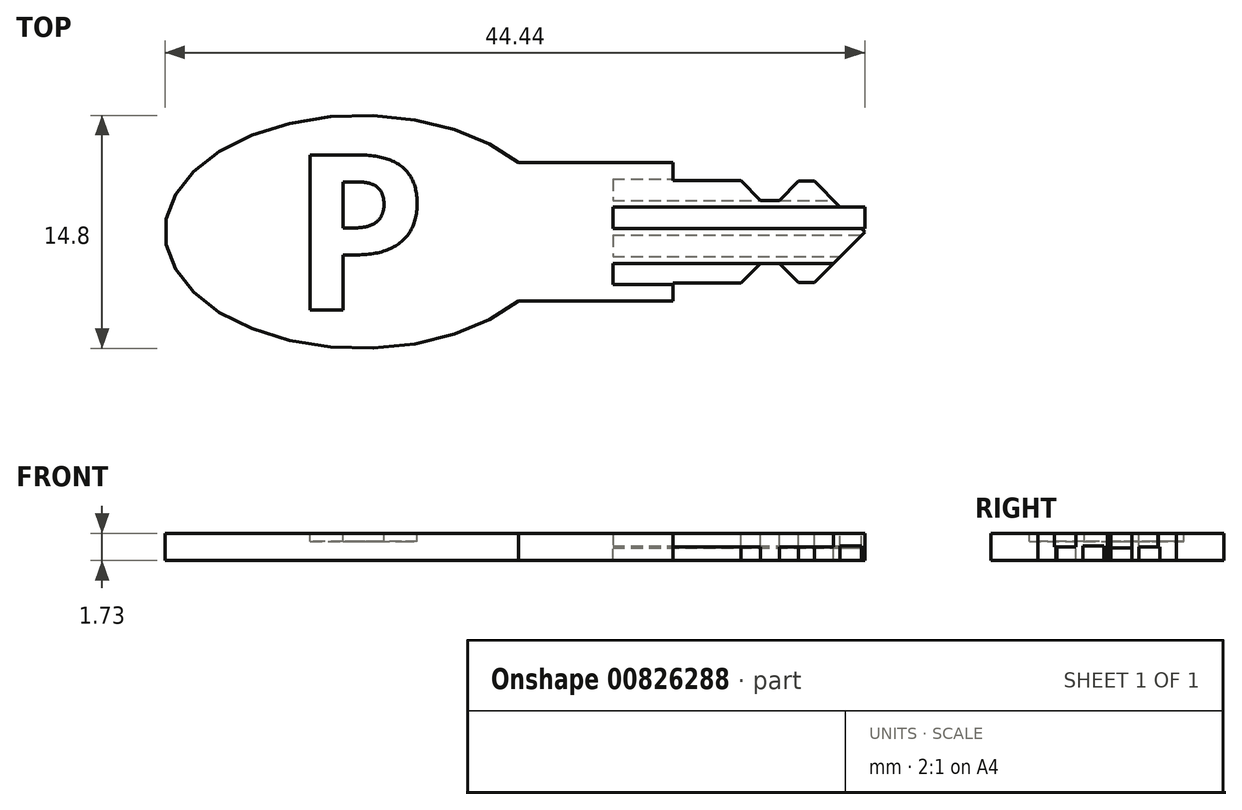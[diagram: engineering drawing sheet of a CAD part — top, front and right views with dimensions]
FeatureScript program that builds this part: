
annotation { "Feature Type Name" : "Feature", "Feature Type Description" : "" }
export const myFeature = defineFeature(function(context is Context, id is Id, definition is map)
    precondition{}
    {
        {
            var Q0;
            Q0=qCreatedBy(makeId("Top.planeOp"),FACE);
            var sketch = newSketch(context, id + "F0", { "sketchPlane" : qUnion([Q0])});
            skLineSegment(sketch, "E0.bottom", {"start": v(-10.25, 4.4) * mm, "end": v(11.75, 4.4) * mm});
            skLineSegment(sketch, "E0.top", {"start": v(-10.25, -4.4) * mm, "end": v(11.75, -4.4) * mm});
            skLineSegment(sketch, "E0.left", {"start": v(-10.25, 4.4) * mm, "end": v(-10.25, -4.4) * mm});
            skLineSegment(sketch, "E0.right", {"start": v(11.75, 4.4) * mm, "end": v(11.75, -4.4) * mm});
            skPoint(sketch, "E1", {"position": v(11.75, 0) * mm});
            skSolve(sketch);
        }
        {
            var Q0;
            Q0 = qSketchRegion(id + "F0", true);
            extrude(context, id + "F1", {"entities" : qUnion([Q0]), "depth" : 1.73 * mm, "offsetDistance" : 25 * mm});
        }
        {
            var Q0;
            Q0=makeQuery(id+"F1.opExtrude","SWEPT_FACE",FACE,{"disambiguationData":[OSD([sQuery(id+"F0.wireOp",EDGE,"E0.right")])]});
            var sketch = newSketch(context, id + "F2", { "sketchPlane" : qUnion([Q0])});
            skLineSegment(sketch, "E2.bottom", {"start": v(-3.35, 1.73) * mm, "end": v(-2, 1.73) * mm});
            skLineSegment(sketch, "E2.top", {"start": v(-3.35, 0.85) * mm, "end": v(-2, 0.85) * mm});
            skLineSegment(sketch, "E2.left", {"start": v(-3.35, 1.73) * mm, "end": v(-3.35, 0.85) * mm});
            skLineSegment(sketch, "E2.right", {"start": v(-2, 1.73) * mm, "end": v(-2, 0.85) * mm});
            skLineSegment(sketch, "E3.bottom", {"start": v(-1.57, 0) * mm, "end": v(-0.22, 0) * mm});
            skLineSegment(sketch, "E3.top", {"start": v(-1.57, 0.93) * mm, "end": v(-0.22, 0.93) * mm});
            skLineSegment(sketch, "E3.left", {"start": v(-1.57, 0) * mm, "end": v(-1.57, 0.93) * mm});
            skLineSegment(sketch, "E3.right", {"start": v(-0.22, 0) * mm, "end": v(-0.22, 0.93) * mm});
            skLineSegment(sketch, "E4.bottom", {"start": v(0.22, 1.73) * mm, "end": v(1.57, 1.73) * mm});
            skLineSegment(sketch, "E4.top", {"start": v(0.22, 0.8) * mm, "end": v(1.57, 0.8) * mm});
            skLineSegment(sketch, "E4.left", {"start": v(0.22, 1.73) * mm, "end": v(0.22, 0.8) * mm});
            skLineSegment(sketch, "E4.right", {"start": v(1.57, 1.73) * mm, "end": v(1.57, 0.8) * mm});
            skLineSegment(sketch, "E5.bottom", {"start": v(3.35, 0) * mm, "end": v(2, 0) * mm});
            skLineSegment(sketch, "E5.top", {"start": v(3.35, 0.88) * mm, "end": v(2, 0.88) * mm});
            skLineSegment(sketch, "E5.left", {"start": v(3.35, 0) * mm, "end": v(3.35, 0.88) * mm});
            skLineSegment(sketch, "E5.right", {"start": v(2, 0) * mm, "end": v(2, 0.88) * mm});
            skLineSegment(sketch, "E6", {"start": v(-0.22, 0.75) * mm, "end": v(0, 0.75) * mm, "construction": true});
            skLineSegment(sketch, "E7", {"start": v(0, 1.3) * mm, "end": v(0.22, 1.3) * mm, "construction": true});
            skLineSegment(sketch, "E8", {"start": v(-1.57, 0.89) * mm, "end": v(-2, 0.89) * mm, "construction": true});
            skLineSegment(sketch, "E9", {"start": v(-0.22, 0.89) * mm, "end": v(0.22, 0.89) * mm, "construction": true});
            skLineSegment(sketch, "E10", {"start": v(1.57, 0.85) * mm, "end": v(2, 0.85) * mm, "construction": true});
            skLineSegment(sketch, "E11", {"start": v(2, 0.85) * mm, "end": v(2, 0.83) * mm, "construction": true});
            skSolve(sketch);
        }
        {
            var Q0;
            Q0 = qSketchRegion(id + "F2", true);
            extrude(context, id + "F3", {"entities" : qUnion([Q0]), "operationType" : NewBodyOperationType.REMOVE, "oppositeDirection" : true, "depth" : 16 * mm, "offsetDistance" : 25 * mm});
        }
        {
            var Q0;
            Q0=makeQuery(id+"F1.opExtrude","CAP_FACE",FACE,{"disambiguationData":[OSD([sQuery(id+"F0.wireOp",EDGE,"E0.bottom"),sQuery(id+"F0.wireOp",EDGE,"E0.top"),sQuery(id+"F0.wireOp",EDGE,"E0.left"),sQuery(id+"F0.wireOp",EDGE,"E0.right")])],"isStart":false});
            var sketch = newSketch(context, id + "F4", { "sketchPlane" : qUnion([Q0])});
            skLineSegment(sketch, "E12", {"start": v(-10.25, 4.4) * mm, "end": v(-0.43, 4.4) * mm});
            skLineSegment(sketch, "E13", {"start": v(-0.43, 4.4) * mm, "end": v(-0.43, 3.25) * mm});
            skLineSegment(sketch, "E14", {"start": v(-0.43, 3.25) * mm, "end": v(2.48, 3.25) * mm});
            skLineSegment(sketch, "E15", {"start": v(2.48, 3.25) * mm, "end": v(3.87, 3.25) * mm});
            skLineSegment(sketch, "E16", {"start": v(3.87, 3.25) * mm, "end": v(5.12, 2) * mm});
            skLineSegment(sketch, "E17", {"start": v(5.12, 2) * mm, "end": v(6.32, 2) * mm});
            skLineSegment(sketch, "E18", {"start": v(6.32, 2) * mm, "end": v(7.53, 3.21) * mm});
            skLineSegment(sketch, "E19", {"start": v(7.53, 3.21) * mm, "end": v(8.53, 3.21) * mm});
            skLineSegment(sketch, "E20", {"start": v(8.53, 3.21) * mm, "end": v(11.75, 0) * mm});
            skLineSegment(sketch, "E21.MirrorCS", {"start": v(-10.25, -4.4) * mm, "end": v(-0.43, -4.4) * mm});
            skLineSegment(sketch, "E22.MirrorCS", {"start": v(-0.43, -4.4) * mm, "end": v(-0.43, -3.25) * mm});
            skLineSegment(sketch, "E23.MirrorCS", {"start": v(-0.43, -3.25) * mm, "end": v(2.48, -3.25) * mm});
            skLineSegment(sketch, "E24.MirrorCS", {"start": v(2.48, -3.25) * mm, "end": v(3.87, -3.25) * mm});
            skLineSegment(sketch, "E25.MirrorCS", {"start": v(3.87, -3.25) * mm, "end": v(5.12, -2) * mm});
            skLineSegment(sketch, "E26.MirrorCS", {"start": v(5.12, -2) * mm, "end": v(6.32, -2) * mm});
            skLineSegment(sketch, "E27.MirrorCS", {"start": v(6.32, -2) * mm, "end": v(7.53, -3.21) * mm});
            skLineSegment(sketch, "E28.MirrorCS", {"start": v(7.53, -3.21) * mm, "end": v(8.53, -3.21) * mm});
            skLineSegment(sketch, "E29.MirrorCS", {"start": v(8.53, -3.21) * mm, "end": v(11.75, 0) * mm});
            skLineSegment(sketch, "E30", {"start": v(-0.43, -4.4) * mm, "end": v(11.75, -4.4) * mm});
            skLineSegment(sketch, "E31", {"start": v(11.75, -4.4) * mm, "end": v(11.75, 0) * mm});
            skLineSegment(sketch, "E32", {"start": v(11.75, 0) * mm, "end": v(11.75, 4.4) * mm});
            skLineSegment(sketch, "E33", {"start": v(11.75, 4.4) * mm, "end": v(-0.43, 4.4) * mm});
            skSolve(sketch);
        }
        {
            var Q0;
            {var subQ0=sQuery(id+"F4.wireOp",EDGE,"E13");Q0=makeQuery(id+"F4.imprint","IMPRINT",FACE,{"disambiguationData":[TD([[makeQuery(id+"F4.imprint","IMPRINT",EDGE,{"derivedFrom":subQ0}),1.0]])]});}
            var Q1;
            {var subQ4=sQuery(id+"F4.wireOp",EDGE,"E22.MirrorCS");Q1=makeQuery(id+"F4.imprint","IMPRINT",FACE,{"disambiguationData":[TD([[makeQuery(id+"F4.imprint","IMPRINT",EDGE,{"derivedFrom":subQ4}),-1.0]])]});}
            var Q2;
            {var subQ12=sQuery(id+"F4.wireOp",EDGE,"E23.MirrorCS");Q2=makeQuery(id+"F4.imprint","IMPRINT",FACE,{"disambiguationData":[TD([[makeQuery(id+"F4.imprint","IMPRINT",EDGE,{"derivedFrom":subQ12}),-1.0]])]});}
            var Q3;
            {var subQ0=sQuery(id+"F4.wireOp",EDGE,"E26.MirrorCS");Q3=makeQuery(id+"F4.imprint","IMPRINT",FACE,{"disambiguationData":[TD([[makeQuery(id+"F4.imprint","IMPRINT",EDGE,{"derivedFrom":subQ0}),-1.0]])]});}
            var Q4;
            {var subQ0=sQuery(id+"F4.wireOp",EDGE,"E31");var subQ1=sQuery(id+"F4.wireOp",EDGE,"E29.MirrorCS");var subQ2=makeQuery(id+"F4.imprint","INTERSECT",VERTEX,{"derivedFrom":[sQuery(id+"F4.wireOp",EDGE,"E20"),subQ1,subQ0,sQuery(id+"F4.wireOp",EDGE,"E32")]});Q4=makeQuery(id+"F4.imprint","IMPRINT",FACE,{"disambiguationData":[TD([[makeQuery(id+"F4.imprint","IMPRINT",EDGE,{"disambiguationData":[TD([[subQ2,1.0]])],"derivedFrom":subQ1}),-1.0]])]});}
            var Q5;
            {var subQ0=sQuery(id+"F4.wireOp",EDGE,"E20");var subQ1=sQuery(id+"F2.wireOp",EDGE,"E4.bottom");var subQ2=sQuery(id+"F0.wireOp",EDGE,"E0.right");var subQ3=makeQuery(id+"F3.boolean.opBoolean","COPY",EDGE,{"derivedFrom":makeQuery(id+"F3.opExtrude","SWEPT_EDGE",EDGE,{"disambiguationData":[OSD([subQ2,subQ1,sQuery(id+"F2.wireOp",EDGE,"E4.right")])]})});var subQ4=makeQuery(id+"F4.imprint","INTERSECT",VERTEX,{"derivedFrom":[subQ3,subQ0]});Q5=makeQuery(id+"F4.imprint","IMPRINT",FACE,{"disambiguationData":[TD([[makeQuery(id+"F4.imprint","IMPRINT",EDGE,{"disambiguationData":[TD([[subQ4,-1.0]])],"derivedFrom":subQ0}),1.0]])]});}
            var Q6;
            {var subQ0=sQuery(id+"F4.wireOp",EDGE,"E32");var subQ1=sQuery(id+"F4.wireOp",EDGE,"E20");var subQ2=makeQuery(id+"F4.imprint","INTERSECT",VERTEX,{"derivedFrom":[subQ1,sQuery(id+"F4.wireOp",EDGE,"E29.MirrorCS"),sQuery(id+"F4.wireOp",EDGE,"E31"),subQ0]});Q6=makeQuery(id+"F4.imprint","IMPRINT",FACE,{"disambiguationData":[TD([[makeQuery(id+"F4.imprint","IMPRINT",EDGE,{"disambiguationData":[TD([[subQ2,1.0]])],"derivedFrom":subQ1}),1.0]])]});}
            var Q7;
            Q7=makeQuery(id+"F1.opExtrude","CAP_FACE",FACE,{"disambiguationData":[OSD([sQuery(id+"F0.wireOp",EDGE,"E0.bottom"),sQuery(id+"F0.wireOp",EDGE,"E0.top"),sQuery(id+"F0.wireOp",EDGE,"E0.left"),sQuery(id+"F0.wireOp",EDGE,"E0.right")])],"isStart":true});
            extrude(context, id + "F5", {"entities" : qUnion([Q0, Q1, Q2, Q3, Q4, Q5, Q6]), "operationType" : NewBodyOperationType.REMOVE, "endBound" : BoundingType.UP_TO_SURFACE, "oppositeDirection" : true, "depth" : 25 * mm, "endBoundEntityFace" : qUnion([Q7]), "offsetDistance" : 25 * mm});
        }
        {
            var Q0;
            Q0=makeQuery(id+"F1.opExtrude","CAP_FACE",FACE,{"disambiguationData":[OSD([sQuery(id+"F0.wireOp",EDGE,"E0.bottom"),sQuery(id+"F0.wireOp",EDGE,"E0.top"),sQuery(id+"F0.wireOp",EDGE,"E0.left"),sQuery(id+"F0.wireOp",EDGE,"E0.right")])],"isStart":true});
            var sketch = newSketch(context, id + "F6", { "sketchPlane" : qUnion([Q0])});
            skEllipse(sketch, "E34", {"center": v(-20.25, 0) * mm, "majorRadius": 12.44 * mm, "minorRadius": 7.4 * mm, "majorAxis": v(1, 0)});
            skSolve(sketch);
        }
        {
            var Q0;
            Q0 = qSketchRegion(id + "F6", true);
            var Q1;
            Q1=makeQuery(id+"F1.opExtrude","CAP_FACE",FACE,{"disambiguationData":[OSD([sQuery(id+"F0.wireOp",EDGE,"E0.bottom"),sQuery(id+"F0.wireOp",EDGE,"E0.top"),sQuery(id+"F0.wireOp",EDGE,"E0.left"),sQuery(id+"F0.wireOp",EDGE,"E0.right")])],"isStart":false});
            extrude(context, id + "F7", {"entities" : qUnion([Q0]), "operationType" : NewBodyOperationType.ADD, "endBound" : BoundingType.UP_TO_SURFACE, "oppositeDirection" : true, "depth" : 25 * mm, "endBoundEntityFace" : qUnion([Q1]), "offsetDistance" : 25 * mm});
        }
        {
            var Q0;
            {var subQ0=sQuery(id+"F0.wireOp",EDGE,"E0.right");var subQ1=sQuery(id+"F0.wireOp",EDGE,"E0.left");var subQ2=sQuery(id+"F0.wireOp",EDGE,"E0.top");var subQ3=sQuery(id+"F0.wireOp",EDGE,"E0.bottom");Q0=makeQuery(id+"F7.boolean.opBoolean","MERGE",FACE,{"derivedFrom":[makeQuery(id+"F1.opExtrude","CAP_FACE",FACE,{"disambiguationData":[OSD([subQ3,subQ2,subQ1,subQ0])],"isStart":false}),makeQuery(id+"F7.opExtrude","CAP_FACE",FACE,{"disambiguationData":[OSD([subQ3,subQ2,subQ1,subQ0])],"isStart":false})]});}
            var sketch = newSketch(context, id + "F8", { "sketchPlane" : qUnion([Q0])});
            skText(sketch, "E35", { "text": "P", "fontName": "OpenSans-Bold.ttf"});
            skPoint(sketch, "E36", {"position": v(-24.72, 0) * mm});
            skPoint(sketch, "E37", {"position": v(-20.25, 0) * mm});
            const initialGuessF8  = {"E35": [-0.02472, -0.00496, 1, 0, 0.00992]};
            skSetInitialGuess(sketch, initialGuessF8);
            skSolve(sketch);
        }
        {
            var Q0;
            Q0 = qSketchRegion(id + "F8", true);
            extrude(context, id + "F9", {"entities" : qUnion([Q0]), "operationType" : NewBodyOperationType.REMOVE, "oppositeDirection" : true, "depth" : 0.5 * mm, "offsetDistance" : 25 * mm});
        }
    });
